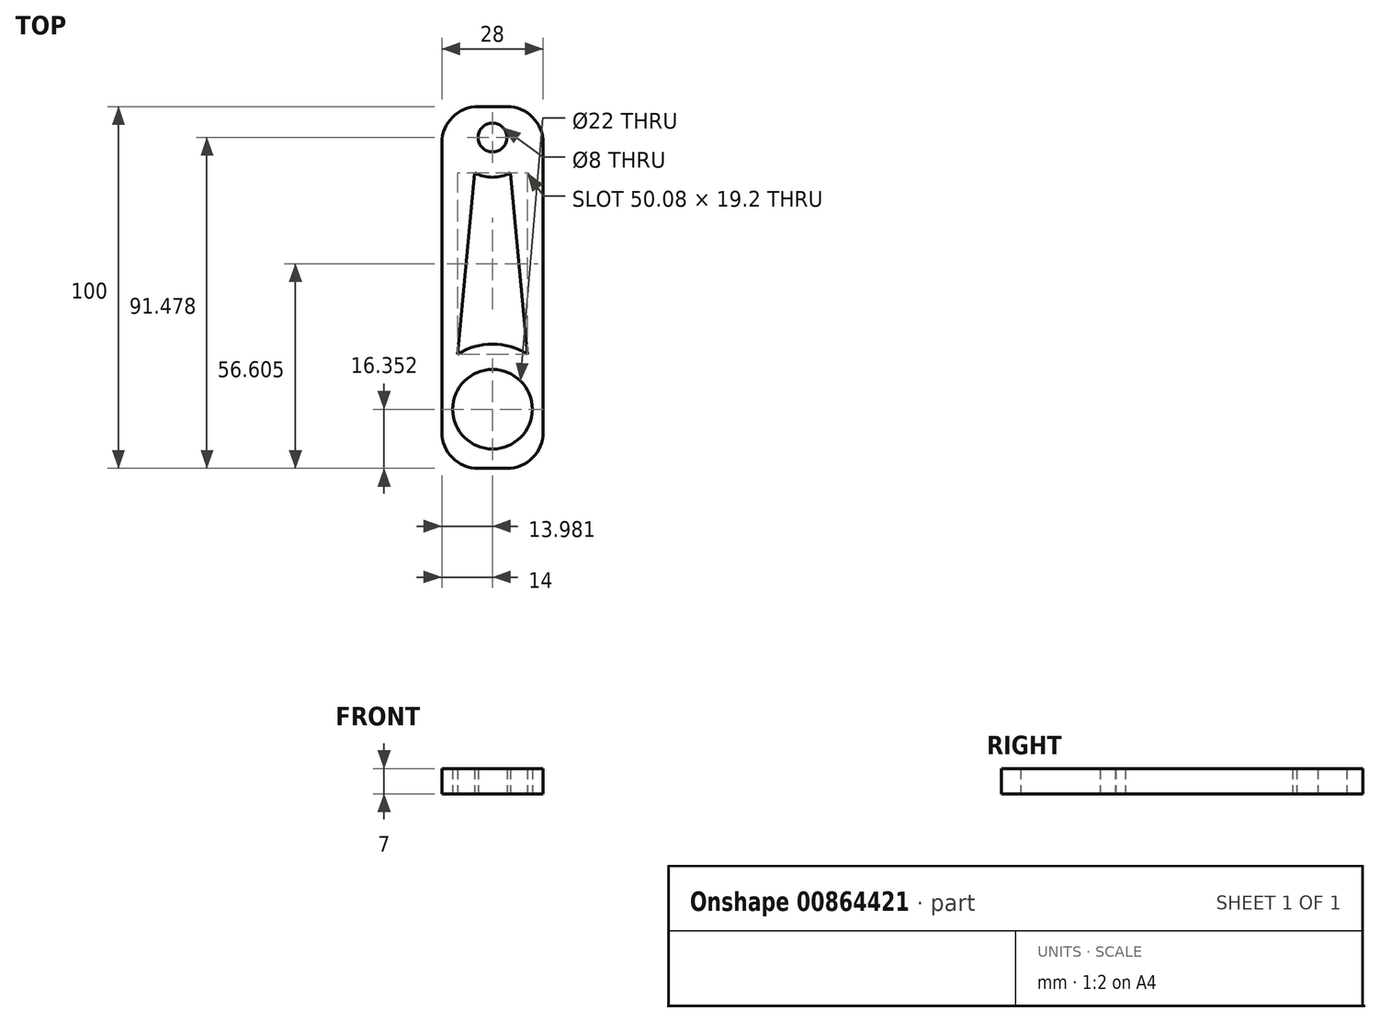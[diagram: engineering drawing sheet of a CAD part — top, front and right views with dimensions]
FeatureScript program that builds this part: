
annotation { "Feature Type Name" : "Feature", "Feature Type Description" : "" }
export const myFeature = defineFeature(function(context is Context, id is Id, definition is map)
    precondition{}
    {
        {
            var Q0;
            Q0=qCreatedBy(makeId("Top.planeOp"),FACE);
            var sketch = newSketch(context, id + "F0", { "sketchPlane" : qUnion([Q0])});
            skLineSegment(sketch, "E0.bottom", {"start": v(-14, 50) * mm, "end": v(14, 50) * mm});
            skLineSegment(sketch, "E0.top", {"start": v(-14, -50) * mm, "end": v(14, -50) * mm});
            skLineSegment(sketch, "E0.left", {"start": v(-14, 50) * mm, "end": v(-14, -50) * mm});
            skLineSegment(sketch, "E0.right", {"start": v(14, 50) * mm, "end": v(14, -50) * mm});
            skPoint(sketch, "E0.middle", {"position": v(0, 0) * mm});
            skCircle(sketch, "E1", {"center": v(0, 41.48) * mm, "radius": 4 * mm});
            skCircle(sketch, "E2", {"center": v(0, -33.65) * mm, "radius": 11 * mm});
            skLineSegment(sketch, "E3", {"start": v(-4, 41.48) * mm, "end": v(-11.05, -33.65) * mm});
            skLineSegment(sketch, "E4", {"start": v(11, -33.65) * mm, "end": v(4.02, 41.48) * mm});
            skCircle(sketch, "E5.0", {"center": v(0, 41.48) * mm, "radius": 11 * mm});
            skCircle(sketch, "E6.0", {"center": v(0, -33.65) * mm, "radius": 18 * mm});
            skSolve(sketch);
        }
        {
            var Q0;
            Q0=makeQuery(id+"F0.imprint","IMPRINT",FACE,{"disambiguationData":[TD([[makeQuery(id+"F0.imprint","IMPRINT",EDGE,{"derivedFrom":sQuery(id+"F0.wireOp",EDGE,"E0.bottom")}),-1.0]])]});
            var Q1;
            {var subQ0=sQuery(id+"F0.wireOp",EDGE,"E6.0");var subQ5=sQuery(id+"F0.wireOp",EDGE,"E0.top");var subQ6=makeQuery(id+"F0.imprint","INTERSECT",VERTEX,{"disambiguationData":[OD(0.0)],"derivedFrom":[subQ5,subQ0]});Q1=makeQuery(id+"F0.imprint","IMPRINT",FACE,{"disambiguationData":[TD([[makeQuery(id+"F0.imprint","IMPRINT",EDGE,{"disambiguationData":[TD([[subQ6,-1.0]])],"derivedFrom":subQ5}),1.0]])]});}
            var Q2;
            {var subQ0=sQuery(id+"F0.wireOp",EDGE,"E3");var subQ1=sQuery(id+"F0.wireOp",EDGE,"E2");var subQ2=makeQuery(id+"F0.imprint","INTERSECT",VERTEX,{"derivedFrom":[subQ1,subQ0]});Q2=makeQuery(id+"F0.imprint","IMPRINT",FACE,{"disambiguationData":[TD([[makeQuery(id+"F0.imprint","IMPRINT",EDGE,{"disambiguationData":[TD([[subQ2,1.0]])],"derivedFrom":subQ1}),-1.0]])]});}
            var Q3;
            {var subQ0=sQuery(id+"F0.wireOp",EDGE,"E0.left");var subQ1=sQuery(id+"F0.wireOp",EDGE,"E0.top");var subQ2=makeQuery(id+"F0.imprint","INTERSECT",VERTEX,{"derivedFrom":[subQ1,subQ0]});Q3=makeQuery(id+"F0.imprint","IMPRINT",FACE,{"disambiguationData":[TD([[makeQuery(id+"F0.imprint","IMPRINT",EDGE,{"disambiguationData":[TD([[subQ2,-1.0]])],"derivedFrom":subQ1}),1.0]])]});}
            var Q4;
            {var subQ0=sQuery(id+"F0.wireOp",EDGE,"E0.right");var subQ1=sQuery(id+"F0.wireOp",EDGE,"E0.top");var subQ2=makeQuery(id+"F0.imprint","INTERSECT",VERTEX,{"derivedFrom":[subQ1,subQ0]});Q4=makeQuery(id+"F0.imprint","IMPRINT",FACE,{"disambiguationData":[TD([[makeQuery(id+"F0.imprint","IMPRINT",EDGE,{"disambiguationData":[TD([[subQ2,1.0]])],"derivedFrom":subQ1}),1.0]])]});}
            extrude(context, id + "F1", {"entities" : qUnion([Q0, Q1, Q2, Q3, Q4]), "depth" : 7 * mm, "offsetDistance" : 25 * mm});
        }
        {
            var Q0;
            Q0=makeQuery(id+"F1.opExtrude","SWEPT_EDGE",EDGE,{"disambiguationData":[OSD([sQuery(id+"F0.wireOp",EDGE,"E0.bottom"),sQuery(id+"F0.wireOp",EDGE,"E0.right")])]});
            var Q1;
            Q1=makeQuery(id+"F1.opExtrude","SWEPT_EDGE",EDGE,{"disambiguationData":[OSD([sQuery(id+"F0.wireOp",EDGE,"E0.bottom"),sQuery(id+"F0.wireOp",EDGE,"E0.left")])]});
            var Q2;
            Q2=makeQuery(id+"F1.opExtrude","SWEPT_EDGE",EDGE,{"disambiguationData":[OSD([sQuery(id+"F0.wireOp",EDGE,"E0.top"),sQuery(id+"F0.wireOp",EDGE,"E0.left")])]});
            var Q3;
            Q3=makeQuery(id+"F1.opExtrude","SWEPT_EDGE",EDGE,{"disambiguationData":[OSD([sQuery(id+"F0.wireOp",EDGE,"E0.top"),sQuery(id+"F0.wireOp",EDGE,"E0.right")])]});
            fillet(context, id + "F2", {"entities" : qUnion([Q0, Q1, Q2, Q3]), "radius" : 10 * mm, "tangentPropagation" : true, "allowEdgeOverflow" : false});
        }
    });
